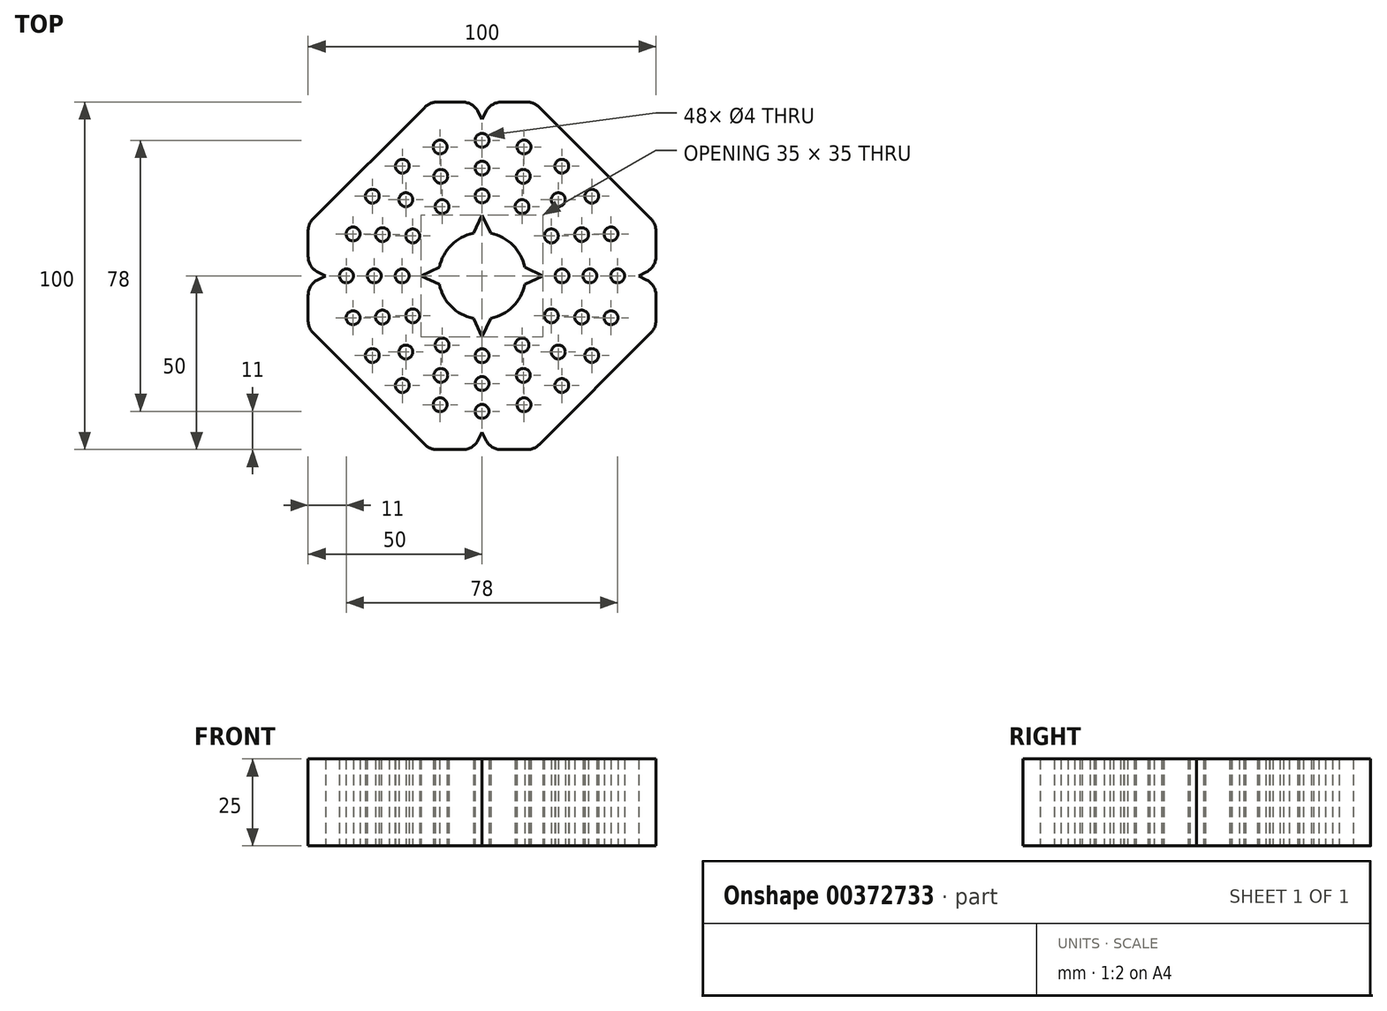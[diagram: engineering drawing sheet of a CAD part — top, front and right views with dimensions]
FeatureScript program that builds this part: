
annotation { "Feature Type Name" : "Feature", "Feature Type Description" : "" }
export const myFeature = defineFeature(function(context is Context, id is Id, definition is map)
    precondition{}
    {
        {
            var Q0;
            Q0=qCreatedBy(makeId("Top.planeOp"),FACE);
            var sketch = newSketch(context, id + "F0", { "sketchPlane" : qUnion([Q0])});
            skCircle(sketch, "E0", {"center": v(0, 23) * mm, "radius": 2 * mm});
            skCircle(sketch, "E1.1.0", {"center": v(-11.5, 19.92) * mm, "radius": 2 * mm});
            skCircle(sketch, "E1.2.0", {"center": v(-19.92, 11.5) * mm, "radius": 2 * mm});
            skCircle(sketch, "E1.3.0", {"center": v(-23, 0) * mm, "radius": 2 * mm});
            skCircle(sketch, "E1.4.0", {"center": v(-19.92, -11.5) * mm, "radius": 2 * mm});
            skCircle(sketch, "E1.5.0", {"center": v(-11.5, -19.92) * mm, "radius": 2 * mm});
            skCircle(sketch, "E1.6.0", {"center": v(0, -23) * mm, "radius": 2 * mm});
            skCircle(sketch, "E1.7.0", {"center": v(11.5, -19.92) * mm, "radius": 2 * mm});
            skCircle(sketch, "E1.8.0", {"center": v(19.92, -11.5) * mm, "radius": 2 * mm});
            skCircle(sketch, "E1.9.0", {"center": v(23, 0) * mm, "radius": 2 * mm});
            skCircle(sketch, "E1.10.0", {"center": v(19.92, 11.5) * mm, "radius": 2 * mm});
            skCircle(sketch, "E1.11.0", {"center": v(11.5, 19.92) * mm, "radius": 2 * mm});
            skPoint(sketch, "E1.center", {"position": v(0, 0) * mm});
            skCircle(sketch, "E2", {"center": v(0, 31) * mm, "radius": 2 * mm});
            skCircle(sketch, "E3.1.0", {"center": v(-11.86, 28.64) * mm, "radius": 2 * mm});
            skCircle(sketch, "E3.2.0", {"center": v(-21.92, 21.92) * mm, "radius": 2 * mm});
            skCircle(sketch, "E3.3.0", {"center": v(-28.64, 11.86) * mm, "radius": 2 * mm});
            skCircle(sketch, "E3.4.0", {"center": v(-31, 0) * mm, "radius": 2 * mm});
            skCircle(sketch, "E3.5.0", {"center": v(-28.64, -11.86) * mm, "radius": 2 * mm});
            skCircle(sketch, "E3.6.0", {"center": v(-21.92, -21.92) * mm, "radius": 2 * mm});
            skCircle(sketch, "E3.7.0", {"center": v(-11.86, -28.64) * mm, "radius": 2 * mm});
            skCircle(sketch, "E3.8.0", {"center": v(0, -31) * mm, "radius": 2 * mm});
            skCircle(sketch, "E3.9.0", {"center": v(11.86, -28.64) * mm, "radius": 2 * mm});
            skCircle(sketch, "E3.10.0", {"center": v(21.92, -21.92) * mm, "radius": 2 * mm});
            skCircle(sketch, "E3.11.0", {"center": v(28.64, -11.86) * mm, "radius": 2 * mm});
            skCircle(sketch, "E3.12.0", {"center": v(31, 0) * mm, "radius": 2 * mm});
            skCircle(sketch, "E3.13.0", {"center": v(28.64, 11.86) * mm, "radius": 2 * mm});
            skCircle(sketch, "E3.14.0", {"center": v(21.92, 21.92) * mm, "radius": 2 * mm});
            skCircle(sketch, "E3.15.0", {"center": v(11.86, 28.64) * mm, "radius": 2 * mm});
            skCircle(sketch, "E4", {"center": v(0, 39) * mm, "radius": 2 * mm});
            skCircle(sketch, "E5.1.0", {"center": v(-12.05, 37.1) * mm, "radius": 2 * mm});
            skCircle(sketch, "E5.2.0", {"center": v(-22.92, 31.55) * mm, "radius": 2 * mm});
            skCircle(sketch, "E5.3.0", {"center": v(-31.55, 22.92) * mm, "radius": 2 * mm});
            skCircle(sketch, "E5.4.0", {"center": v(-37.1, 12.05) * mm, "radius": 2 * mm});
            skCircle(sketch, "E5.5.0", {"center": v(-39, 0) * mm, "radius": 2 * mm});
            skCircle(sketch, "E5.6.0", {"center": v(-37.1, -12.05) * mm, "radius": 2 * mm});
            skCircle(sketch, "E5.7.0", {"center": v(-31.55, -22.92) * mm, "radius": 2 * mm});
            skCircle(sketch, "E5.8.0", {"center": v(-22.92, -31.55) * mm, "radius": 2 * mm});
            skCircle(sketch, "E5.9.0", {"center": v(-12.05, -37.1) * mm, "radius": 2 * mm});
            skCircle(sketch, "E5.10.0", {"center": v(0, -39) * mm, "radius": 2 * mm});
            skCircle(sketch, "E5.11.0", {"center": v(12.05, -37.1) * mm, "radius": 2 * mm});
            skCircle(sketch, "E5.12.0", {"center": v(22.92, -31.55) * mm, "radius": 2 * mm});
            skCircle(sketch, "E5.13.0", {"center": v(31.55, -22.92) * mm, "radius": 2 * mm});
            skCircle(sketch, "E5.14.0", {"center": v(37.1, -12.05) * mm, "radius": 2 * mm});
            skCircle(sketch, "E5.15.0", {"center": v(39, 0) * mm, "radius": 2 * mm});
            skCircle(sketch, "E5.16.0", {"center": v(37.1, 12.05) * mm, "radius": 2 * mm});
            skCircle(sketch, "E5.17.0", {"center": v(31.55, 22.92) * mm, "radius": 2 * mm});
            skCircle(sketch, "E5.18.0", {"center": v(22.92, 31.55) * mm, "radius": 2 * mm});
            skCircle(sketch, "E5.19.0", {"center": v(12.05, 37.1) * mm, "radius": 2 * mm});
            skArc(sketch, "E6", {"start": v(-2.5, 12.25) * mm, "mid": v(-8.84, 8.84) * mm, "end": v(-12.25, 2.5) * mm});
            skLineSegment(sketch, "E7.bottom", {"start": v(-12.93, 50) * mm, "end": v(-5.6, 50) * mm});
            skLineSegment(sketch, "E7.top", {"start": v(-12.93, -50) * mm, "end": v(-5.6, -50) * mm});
            skLineSegment(sketch, "E7.left", {"start": v(-50, 12.93) * mm, "end": v(-50, 5.6) * mm});
            skLineSegment(sketch, "E7.right", {"start": v(50, 12.93) * mm, "end": v(50, 5.6) * mm});
            skLineSegment(sketch, "E8", {"start": v(-45, 0) * mm, "end": v(-47.24, 1.12) * mm});
            skLineSegment(sketch, "E9.MirrorCS", {"start": v(-45, 0) * mm, "end": v(-47.24, -1.12) * mm});
            skLineSegment(sketch, "E10.trimOffspring", {"start": v(-50, -5.6) * mm, "end": v(-50, -12.93) * mm});
            skLineSegment(sketch, "E11.1.0", {"start": v(0, -45) * mm, "end": v(-1.12, -47.24) * mm});
            skLineSegment(sketch, "E11.1.1", {"start": v(0, -45) * mm, "end": v(1.12, -47.24) * mm});
            skLineSegment(sketch, "E11.2.0", {"start": v(45, 0) * mm, "end": v(47.24, -1.12) * mm});
            skLineSegment(sketch, "E11.2.1", {"start": v(45, 0) * mm, "end": v(47.24, 1.12) * mm});
            skLineSegment(sketch, "E11.3.0", {"start": v(0, 45) * mm, "end": v(1.12, 47.24) * mm});
            skLineSegment(sketch, "E11.3.1", {"start": v(0, 45) * mm, "end": v(-1.12, 47.24) * mm});
            skLineSegment(sketch, "E12.trimOffspring", {"start": v(5.6, 50) * mm, "end": v(12.93, 50) * mm});
            skLineSegment(sketch, "E13.trimOffspring", {"start": v(50, -5.6) * mm, "end": v(50, -12.93) * mm});
            skLineSegment(sketch, "E14.trimOffspring", {"start": v(5.6, -50) * mm, "end": v(12.93, -50) * mm});
            skLineSegment(sketch, "E15", {"start": v(0, 17.5) * mm, "end": v(2.5, 12.25) * mm});
            skLineSegment(sketch, "E16.MirrorCS", {"start": v(0, 17.5) * mm, "end": v(-2.5, 12.25) * mm});
            skLineSegment(sketch, "E17.1.0", {"start": v(-17.5, 0) * mm, "end": v(-12.25, -2.5) * mm});
            skLineSegment(sketch, "E17.1.1", {"start": v(-17.5, 0) * mm, "end": v(-12.25, 2.5) * mm});
            skLineSegment(sketch, "E17.2.0", {"start": v(0, -17.5) * mm, "end": v(2.5, -12.25) * mm});
            skLineSegment(sketch, "E17.2.1", {"start": v(0, -17.5) * mm, "end": v(-2.5, -12.25) * mm});
            skLineSegment(sketch, "E17.3.0", {"start": v(17.5, 0) * mm, "end": v(12.25, 2.5) * mm});
            skLineSegment(sketch, "E17.3.1", {"start": v(17.5, 0) * mm, "end": v(12.25, -2.5) * mm});
            skArc(sketch, "E18.trimOffspring", {"start": v(12.25, 2.5) * mm, "mid": v(8.84, 8.84) * mm, "end": v(2.5, 12.25) * mm});
            skArc(sketch, "E19.trimOffspring", {"start": v(2.5, -12.25) * mm, "mid": v(8.84, -8.84) * mm, "end": v(12.25, -2.5) * mm});
            skArc(sketch, "E20.trimOffspring", {"start": v(-12.25, -2.5) * mm, "mid": v(-8.84, -8.84) * mm, "end": v(-2.5, -12.25) * mm});
            skLineSegment(sketch, "E21", {"start": v(-48.54, 16.46) * mm, "end": v(-16.46, 48.54) * mm});
            skLineSegment(sketch, "E22.MirrorCS", {"start": v(48.54, 16.46) * mm, "end": v(16.46, 48.54) * mm});
            skLineSegment(sketch, "E23.MirrorCS", {"start": v(48.54, -16.46) * mm, "end": v(16.46, -48.54) * mm});
            skLineSegment(sketch, "E24.MirrorCS", {"start": v(-48.54, -16.46) * mm, "end": v(-16.46, -48.54) * mm});
            skPoint(sketch, "E25.visualSharp", {"position": v(-15, 50) * mm});
            skArc(sketch, "E25.filletArc", {"start": v(-12.93, 50) * mm, "mid": v(-14.84, 49.62) * mm, "end": v(-16.46, 48.54) * mm});
            skPoint(sketch, "E26.visualSharp", {"position": v(-2.5, 50) * mm});
            skArc(sketch, "E26.filletArc", {"start": v(-1.12, 47.24) * mm, "mid": v(-2.96, 49.25) * mm, "end": v(-5.6, 50) * mm});
            skPoint(sketch, "E27.visualSharp", {"position": v(2.5, 50) * mm});
            skArc(sketch, "E27.filletArc", {"start": v(5.6, 50) * mm, "mid": v(2.96, 49.25) * mm, "end": v(1.12, 47.24) * mm});
            skPoint(sketch, "E28.visualSharp", {"position": v(15, 50) * mm});
            skArc(sketch, "E28.filletArc", {"start": v(16.46, 48.54) * mm, "mid": v(14.84, 49.62) * mm, "end": v(12.93, 50) * mm});
            skPoint(sketch, "E29.visualSharp", {"position": v(50, 15) * mm});
            skArc(sketch, "E29.filletArc", {"start": v(50, 12.93) * mm, "mid": v(49.62, 14.84) * mm, "end": v(48.54, 16.46) * mm});
            skPoint(sketch, "E30.visualSharp", {"position": v(50, 2.5) * mm});
            skArc(sketch, "E30.filletArc", {"start": v(47.24, 1.12) * mm, "mid": v(49.25, 2.96) * mm, "end": v(50, 5.6) * mm});
            skPoint(sketch, "E31.visualSharp", {"position": v(50, -2.5) * mm});
            skArc(sketch, "E31.filletArc", {"start": v(50, -5.6) * mm, "mid": v(49.25, -2.96) * mm, "end": v(47.24, -1.12) * mm});
            skPoint(sketch, "E32.visualSharp", {"position": v(50, -15) * mm});
            skArc(sketch, "E32.filletArc", {"start": v(48.54, -16.46) * mm, "mid": v(49.62, -14.84) * mm, "end": v(50, -12.93) * mm});
            skPoint(sketch, "E33.visualSharp", {"position": v(15, -50) * mm});
            skArc(sketch, "E33.filletArc", {"start": v(12.93, -50) * mm, "mid": v(14.84, -49.62) * mm, "end": v(16.46, -48.54) * mm});
            skPoint(sketch, "E34.visualSharp", {"position": v(2.5, -50) * mm});
            skArc(sketch, "E34.filletArc", {"start": v(1.12, -47.24) * mm, "mid": v(2.96, -49.25) * mm, "end": v(5.6, -50) * mm});
            skPoint(sketch, "E35.visualSharp", {"position": v(-2.5, -50) * mm});
            skArc(sketch, "E35.filletArc", {"start": v(-5.6, -50) * mm, "mid": v(-2.96, -49.25) * mm, "end": v(-1.12, -47.24) * mm});
            skPoint(sketch, "E36.visualSharp", {"position": v(-15, -50) * mm});
            skArc(sketch, "E36.filletArc", {"start": v(-16.46, -48.54) * mm, "mid": v(-14.84, -49.62) * mm, "end": v(-12.93, -50) * mm});
            skPoint(sketch, "E37.visualSharp", {"position": v(-50, -15) * mm});
            skArc(sketch, "E37.filletArc", {"start": v(-50, -12.93) * mm, "mid": v(-49.62, -14.84) * mm, "end": v(-48.54, -16.46) * mm});
            skPoint(sketch, "E38.visualSharp", {"position": v(-50, -2.5) * mm});
            skArc(sketch, "E38.filletArc", {"start": v(-47.24, -1.12) * mm, "mid": v(-49.25, -2.96) * mm, "end": v(-50, -5.6) * mm});
            skPoint(sketch, "E39.visualSharp", {"position": v(-50, 2.5) * mm});
            skArc(sketch, "E39.filletArc", {"start": v(-50, 5.6) * mm, "mid": v(-49.25, 2.96) * mm, "end": v(-47.24, 1.12) * mm});
            skPoint(sketch, "E40.visualSharp", {"position": v(-50, 15) * mm});
            skArc(sketch, "E40.filletArc", {"start": v(-48.54, 16.46) * mm, "mid": v(-49.62, 14.84) * mm, "end": v(-50, 12.93) * mm});
            skSolve(sketch);
        }
        {
            var Q0;
            Q0=makeQuery(id+"F0.imprint","IMPRINT",FACE,{"disambiguationData":[TD([[makeQuery(id+"F0.imprint","IMPRINT",EDGE,{"derivedFrom":sQuery(id+"F0.wireOp",EDGE,"E0")}),-1.0]])]});
            extrude(context, id + "F1", {"entities" : qUnion([Q0]), "depth" : 25 * mm});
        }
    });
